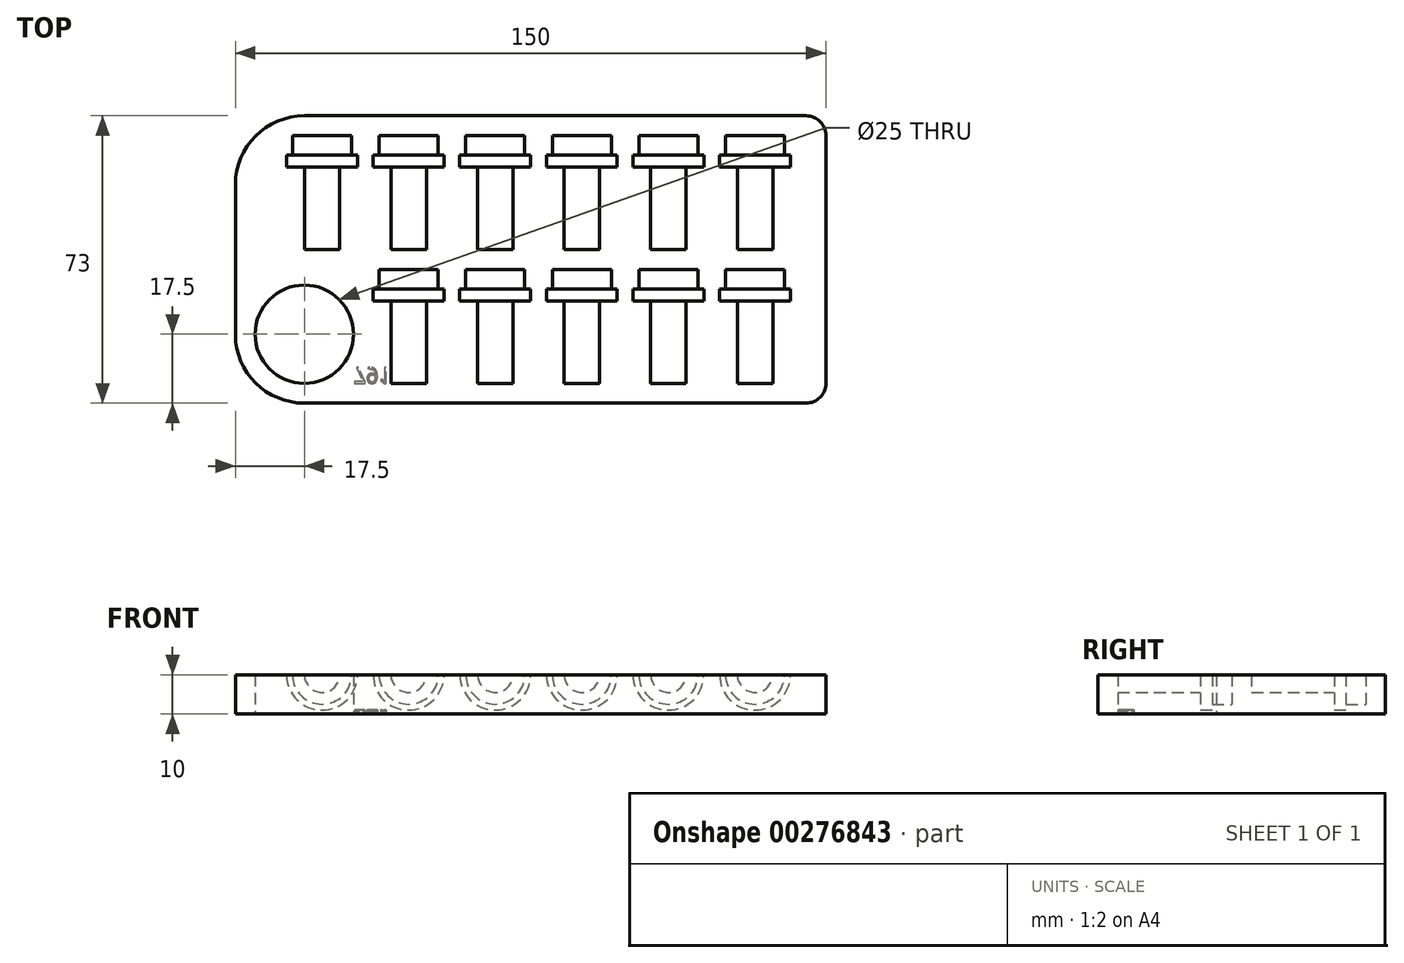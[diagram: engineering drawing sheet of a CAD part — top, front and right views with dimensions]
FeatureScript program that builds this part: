
annotation { "Feature Type Name" : "Feature", "Feature Type Description" : "" }
export const myFeature = defineFeature(function(context is Context, id is Id, definition is map)
    precondition{}
    {
        {
            var Q0;
            Q0=qCreatedBy(makeId("Top.planeOp"),FACE);
            var sketch = newSketch(context, id + "F0", { "sketchPlane" : qUnion([Q0])});
            skLineSegment(sketch, "E0.bottom", {"start": v(17.5, 0) * mm, "end": v(145, 0) * mm});
            skLineSegment(sketch, "E0.top", {"start": v(17.5, 73) * mm, "end": v(145, 73) * mm});
            skLineSegment(sketch, "E0.left", {"start": v(0, 17.5) * mm, "end": v(0, 55.5) * mm});
            skLineSegment(sketch, "E0.right", {"start": v(150, 5) * mm, "end": v(150, 68) * mm});
            skLineSegment(sketch, "E1.bottom", {"start": v(0, 0) * mm, "end": v(17.5, 0) * mm, "construction": true});
            skLineSegment(sketch, "E1.top", {"start": v(0, 17.5) * mm, "end": v(17.5, 17.5) * mm, "construction": true});
            skLineSegment(sketch, "E1.left", {"start": v(0, 0) * mm, "end": v(0, 17.5) * mm, "construction": true});
            skLineSegment(sketch, "E1.right", {"start": v(17.5, 0) * mm, "end": v(17.5, 17.5) * mm, "construction": true});
            skCircle(sketch, "E2", {"center": v(17.5, 17.5) * mm, "radius": 12.5 * mm});
            skPoint(sketch, "E3.visualSharp", {"position": v(0, 0) * mm});
            skArc(sketch, "E3.filletArc", {"start": v(0, 17.5) * mm, "mid": v(5.13, 5.13) * mm, "end": v(17.5, 0) * mm});
            skPoint(sketch, "E4.visualSharp", {"position": v(0, 73) * mm});
            skArc(sketch, "E4.filletArc", {"start": v(17.5, 73) * mm, "mid": v(5.13, 67.87) * mm, "end": v(0, 55.5) * mm});
            skPoint(sketch, "E5.visualSharp", {"position": v(150, 73) * mm});
            skArc(sketch, "E5.filletArc", {"start": v(150, 68) * mm, "mid": v(148.54, 71.54) * mm, "end": v(145, 73) * mm});
            skPoint(sketch, "E6.visualSharp", {"position": v(150, 0) * mm});
            skArc(sketch, "E6.filletArc", {"start": v(145, 0) * mm, "mid": v(148.54, 1.46) * mm, "end": v(150, 5) * mm});
            skSolve(sketch);
        }
        {
            var Q0;
            Q0=makeQuery(id+"F0.imprint","IMPRINT",FACE,{"disambiguationData":[TD([[makeQuery(id+"F0.imprint","IMPRINT",EDGE,{"derivedFrom":sQuery(id+"F0.wireOp",EDGE,"E0.bottom")}),1.0]])]});
            extrude(context, id + "F1", {"entities" : qUnion([Q0]), "depth" : 10 * mm});
        }
        {
            var Q0;
            Q0=makeQuery(id+"F1.opExtrude","CAP_FACE",FACE,{"disambiguationData":[OSD([sQuery(id+"F0.wireOp",EDGE,"E0.bottom"),sQuery(id+"F0.wireOp",EDGE,"E0.top"),sQuery(id+"F0.wireOp",EDGE,"E0.left"),sQuery(id+"F0.wireOp",EDGE,"E0.right"),sQuery(id+"F0.wireOp",EDGE,"E2"),sQuery(id+"F0.wireOp",EDGE,"E3.filletArc"),sQuery(id+"F0.wireOp",EDGE,"E4.filletArc"),sQuery(id+"F0.wireOp",EDGE,"E5.filletArc"),sQuery(id+"F0.wireOp",EDGE,"E6.filletArc")])],"isStart":false});
            var sketch = newSketch(context, id + "F2", { "sketchPlane" : qUnion([Q0])});
            skLineSegment(sketch, "E7.bottom", {"start": v(0, 0) * mm, "end": v(44, 0) * mm, "construction": true});
            skLineSegment(sketch, "E7.top", {"start": v(0, 5) * mm, "end": v(44, 5) * mm, "construction": true});
            skLineSegment(sketch, "E7.left", {"start": v(0, 0) * mm, "end": v(0, 5) * mm, "construction": true});
            skLineSegment(sketch, "E7.right", {"start": v(44, 0) * mm, "end": v(44, 5) * mm, "construction": true});
            skLineSegment(sketch, "E8", {"start": v(44, 5) * mm, "end": v(44, 39) * mm, "construction": true});
            skLineSegment(sketch, "E9", {"start": v(44, 39) * mm, "end": v(66, 39) * mm, "construction": true});
            skLineSegment(sketch, "E10", {"start": v(66, 39) * mm, "end": v(88, 39) * mm, "construction": true});
            skLineSegment(sketch, "E11", {"start": v(44, 39) * mm, "end": v(22, 39) * mm, "construction": true});
            skLineSegment(sketch, "E12", {"start": v(88, 39) * mm, "end": v(110, 39) * mm, "construction": true});
            skLineSegment(sketch, "E13", {"start": v(110, 39) * mm, "end": v(132, 39) * mm, "construction": true});
            skLineSegment(sketch, "E14", {"start": v(44, 5) * mm, "end": v(66, 5) * mm, "construction": true});
            skLineSegment(sketch, "E15", {"start": v(66, 5) * mm, "end": v(88, 5) * mm, "construction": true});
            skLineSegment(sketch, "E16", {"start": v(88, 5) * mm, "end": v(110, 5) * mm, "construction": true});
            skLineSegment(sketch, "E17", {"start": v(110, 5) * mm, "end": v(132, 5) * mm, "construction": true});
            skLineSegment(sketch, "E18.bottom", {"start": v(22, 39) * mm, "end": v(26.5, 39) * mm});
            skLineSegment(sketch, "E18.left", {"start": v(22, 39) * mm, "end": v(22, 60) * mm});
            skLineSegment(sketch, "E18.right", {"start": v(26.5, 39) * mm, "end": v(26.5, 60) * mm});
            skLineSegment(sketch, "E19.bottom", {"start": v(44, 39) * mm, "end": v(48.5, 39) * mm});
            skLineSegment(sketch, "E19.left", {"start": v(44, 39) * mm, "end": v(44, 60) * mm});
            skLineSegment(sketch, "E19.right", {"start": v(48.5, 39) * mm, "end": v(48.5, 60) * mm});
            skLineSegment(sketch, "E20.bottom", {"start": v(66, 39) * mm, "end": v(70.5, 39) * mm});
            skLineSegment(sketch, "E20.left", {"start": v(66, 39) * mm, "end": v(66, 60) * mm});
            skLineSegment(sketch, "E20.right", {"start": v(70.5, 39) * mm, "end": v(70.5, 60) * mm});
            skLineSegment(sketch, "E21.bottom", {"start": v(88, 39) * mm, "end": v(92.5, 39) * mm});
            skLineSegment(sketch, "E21.left", {"start": v(88, 39) * mm, "end": v(88, 60) * mm});
            skLineSegment(sketch, "E21.right", {"start": v(92.5, 39) * mm, "end": v(92.5, 60) * mm});
            skLineSegment(sketch, "E22.bottom", {"start": v(110, 39) * mm, "end": v(114.5, 39) * mm});
            skLineSegment(sketch, "E22.left", {"start": v(110, 39) * mm, "end": v(110, 60) * mm});
            skLineSegment(sketch, "E22.right", {"start": v(114.5, 39) * mm, "end": v(114.5, 60) * mm});
            skLineSegment(sketch, "E23.bottom", {"start": v(132, 39) * mm, "end": v(136.5, 39) * mm});
            skLineSegment(sketch, "E23.left", {"start": v(132, 39) * mm, "end": v(132, 60) * mm});
            skLineSegment(sketch, "E23.right", {"start": v(136.5, 39) * mm, "end": v(136.5, 60) * mm});
            skLineSegment(sketch, "E24.bottom", {"start": v(44, 5) * mm, "end": v(48.5, 5) * mm});
            skLineSegment(sketch, "E24.left", {"start": v(44, 5) * mm, "end": v(44, 26) * mm});
            skLineSegment(sketch, "E24.right", {"start": v(48.5, 5) * mm, "end": v(48.5, 26) * mm});
            skLineSegment(sketch, "E25.bottom", {"start": v(66, 5) * mm, "end": v(70.5, 5) * mm});
            skLineSegment(sketch, "E25.left", {"start": v(66, 5) * mm, "end": v(66, 26) * mm});
            skLineSegment(sketch, "E25.right", {"start": v(70.5, 5) * mm, "end": v(70.5, 26) * mm});
            skLineSegment(sketch, "E26.bottom", {"start": v(88, 5) * mm, "end": v(92.5, 5) * mm});
            skLineSegment(sketch, "E26.left", {"start": v(88, 5) * mm, "end": v(88, 26) * mm});
            skLineSegment(sketch, "E26.right", {"start": v(92.5, 5) * mm, "end": v(92.5, 26) * mm});
            skLineSegment(sketch, "E27.bottom", {"start": v(110, 5) * mm, "end": v(114.5, 5) * mm});
            skLineSegment(sketch, "E27.left", {"start": v(110, 5) * mm, "end": v(110, 26) * mm});
            skLineSegment(sketch, "E27.right", {"start": v(114.5, 5) * mm, "end": v(114.5, 26) * mm});
            skLineSegment(sketch, "E28.bottom", {"start": v(132, 5) * mm, "end": v(136.5, 5) * mm});
            skLineSegment(sketch, "E28.left", {"start": v(132, 5) * mm, "end": v(132, 26) * mm});
            skLineSegment(sketch, "E28.right", {"start": v(136.5, 5) * mm, "end": v(136.5, 26) * mm});
            skLineSegment(sketch, "E29.bottom", {"start": v(26.5, 60) * mm, "end": v(31, 60) * mm});
            skLineSegment(sketch, "E29.top", {"start": v(29.5, 63) * mm, "end": v(31, 63) * mm});
            skLineSegment(sketch, "E29.left", {"start": v(22, 60) * mm, "end": v(22, 63) * mm});
            skLineSegment(sketch, "E29.right", {"start": v(31, 60) * mm, "end": v(31, 63) * mm});
            skLineSegment(sketch, "E30.bottom", {"start": v(48.5, 60) * mm, "end": v(53, 60) * mm});
            skLineSegment(sketch, "E30.top", {"start": v(51.5, 63) * mm, "end": v(53, 63) * mm});
            skLineSegment(sketch, "E30.left", {"start": v(44, 60) * mm, "end": v(44, 63) * mm});
            skLineSegment(sketch, "E30.right", {"start": v(53, 60) * mm, "end": v(53, 63) * mm});
            skLineSegment(sketch, "E31.bottom", {"start": v(70.5, 60) * mm, "end": v(75, 60) * mm});
            skLineSegment(sketch, "E31.top", {"start": v(73.5, 63) * mm, "end": v(75, 63) * mm});
            skLineSegment(sketch, "E31.left", {"start": v(66, 60) * mm, "end": v(66, 63) * mm});
            skLineSegment(sketch, "E31.right", {"start": v(75, 60) * mm, "end": v(75, 63) * mm});
            skLineSegment(sketch, "E32.bottom", {"start": v(92.5, 60) * mm, "end": v(97, 60) * mm});
            skLineSegment(sketch, "E32.top", {"start": v(95.5, 63) * mm, "end": v(97, 63) * mm});
            skLineSegment(sketch, "E32.left", {"start": v(88, 60) * mm, "end": v(88, 63) * mm});
            skLineSegment(sketch, "E32.right", {"start": v(97, 60) * mm, "end": v(97, 63) * mm});
            skLineSegment(sketch, "E33.bottom", {"start": v(114.5, 60) * mm, "end": v(119, 60) * mm});
            skLineSegment(sketch, "E33.top", {"start": v(117.5, 63) * mm, "end": v(119, 63) * mm});
            skLineSegment(sketch, "E33.left", {"start": v(110, 60) * mm, "end": v(110, 63) * mm});
            skLineSegment(sketch, "E33.right", {"start": v(119, 60) * mm, "end": v(119, 63) * mm});
            skLineSegment(sketch, "E34.bottom", {"start": v(136.5, 60) * mm, "end": v(141, 60) * mm});
            skLineSegment(sketch, "E34.top", {"start": v(139.5, 63) * mm, "end": v(141, 63) * mm});
            skLineSegment(sketch, "E34.left", {"start": v(132, 60) * mm, "end": v(132, 63) * mm});
            skLineSegment(sketch, "E34.right", {"start": v(141, 60) * mm, "end": v(141, 63) * mm});
            skLineSegment(sketch, "E35.bottom", {"start": v(48.5, 26) * mm, "end": v(53, 26) * mm});
            skLineSegment(sketch, "E35.top", {"start": v(51.5, 29) * mm, "end": v(53, 29) * mm});
            skLineSegment(sketch, "E35.left", {"start": v(44, 26) * mm, "end": v(44, 29) * mm});
            skLineSegment(sketch, "E35.right", {"start": v(53, 26) * mm, "end": v(53, 29) * mm});
            skLineSegment(sketch, "E36.bottom", {"start": v(70.5, 26) * mm, "end": v(75, 26) * mm});
            skLineSegment(sketch, "E36.top", {"start": v(73.5, 29) * mm, "end": v(75, 29) * mm});
            skLineSegment(sketch, "E36.left", {"start": v(66, 26) * mm, "end": v(66, 29) * mm});
            skLineSegment(sketch, "E36.right", {"start": v(75, 26) * mm, "end": v(75, 29) * mm});
            skLineSegment(sketch, "E37.bottom", {"start": v(92.5, 26) * mm, "end": v(97, 26) * mm});
            skLineSegment(sketch, "E37.top", {"start": v(95.5, 29) * mm, "end": v(97, 29) * mm});
            skLineSegment(sketch, "E37.left", {"start": v(88, 26) * mm, "end": v(88, 29) * mm});
            skLineSegment(sketch, "E37.right", {"start": v(97, 26) * mm, "end": v(97, 29) * mm});
            skLineSegment(sketch, "E38.bottom", {"start": v(114.5, 26) * mm, "end": v(119, 26) * mm});
            skLineSegment(sketch, "E38.top", {"start": v(117.5, 29) * mm, "end": v(119, 29) * mm});
            skLineSegment(sketch, "E38.left", {"start": v(110, 26) * mm, "end": v(110, 29) * mm});
            skLineSegment(sketch, "E38.right", {"start": v(119, 26) * mm, "end": v(119, 29) * mm});
            skLineSegment(sketch, "E39.bottom", {"start": v(136.5, 26) * mm, "end": v(141, 26) * mm});
            skLineSegment(sketch, "E39.top", {"start": v(139.5, 29) * mm, "end": v(141, 29) * mm});
            skLineSegment(sketch, "E39.left", {"start": v(132, 26) * mm, "end": v(132, 29) * mm});
            skLineSegment(sketch, "E39.right", {"start": v(141, 26) * mm, "end": v(141, 29) * mm});
            skLineSegment(sketch, "E40.top", {"start": v(22, 68) * mm, "end": v(29.5, 68) * mm});
            skLineSegment(sketch, "E40.left", {"start": v(22, 63) * mm, "end": v(22, 68) * mm});
            skLineSegment(sketch, "E40.right", {"start": v(29.5, 63) * mm, "end": v(29.5, 68) * mm});
            skLineSegment(sketch, "E41.top", {"start": v(44, 68) * mm, "end": v(51.5, 68) * mm});
            skLineSegment(sketch, "E41.left", {"start": v(44, 63) * mm, "end": v(44, 68) * mm});
            skLineSegment(sketch, "E41.right", {"start": v(51.5, 63) * mm, "end": v(51.5, 68) * mm});
            skLineSegment(sketch, "E42.top", {"start": v(66, 68) * mm, "end": v(73.5, 68) * mm});
            skLineSegment(sketch, "E42.left", {"start": v(66, 63) * mm, "end": v(66, 68) * mm});
            skLineSegment(sketch, "E42.right", {"start": v(73.5, 63) * mm, "end": v(73.5, 68) * mm});
            skLineSegment(sketch, "E43.top", {"start": v(88, 68) * mm, "end": v(95.5, 68) * mm});
            skLineSegment(sketch, "E43.left", {"start": v(88, 63) * mm, "end": v(88, 68) * mm});
            skLineSegment(sketch, "E43.right", {"start": v(95.5, 63) * mm, "end": v(95.5, 68) * mm});
            skLineSegment(sketch, "E44.top", {"start": v(110, 68) * mm, "end": v(117.5, 68) * mm});
            skLineSegment(sketch, "E44.left", {"start": v(110, 63) * mm, "end": v(110, 68) * mm});
            skLineSegment(sketch, "E44.right", {"start": v(117.5, 63) * mm, "end": v(117.5, 68) * mm});
            skLineSegment(sketch, "E45.top", {"start": v(132, 68) * mm, "end": v(139.5, 68) * mm});
            skLineSegment(sketch, "E45.left", {"start": v(132, 63) * mm, "end": v(132, 68) * mm});
            skLineSegment(sketch, "E45.right", {"start": v(139.5, 63) * mm, "end": v(139.5, 68) * mm});
            skLineSegment(sketch, "E46.top", {"start": v(132, 34) * mm, "end": v(139.5, 34) * mm});
            skLineSegment(sketch, "E46.left", {"start": v(132, 29) * mm, "end": v(132, 34) * mm});
            skLineSegment(sketch, "E46.right", {"start": v(139.5, 29) * mm, "end": v(139.5, 34) * mm});
            skLineSegment(sketch, "E47.top", {"start": v(110, 34) * mm, "end": v(117.5, 34) * mm});
            skLineSegment(sketch, "E47.left", {"start": v(110, 29) * mm, "end": v(110, 34) * mm});
            skLineSegment(sketch, "E47.right", {"start": v(117.5, 29) * mm, "end": v(117.5, 34) * mm});
            skLineSegment(sketch, "E48.top", {"start": v(88, 34) * mm, "end": v(95.5, 34) * mm});
            skLineSegment(sketch, "E48.left", {"start": v(88, 29) * mm, "end": v(88, 34) * mm});
            skLineSegment(sketch, "E48.right", {"start": v(95.5, 29) * mm, "end": v(95.5, 34) * mm});
            skLineSegment(sketch, "E49.top", {"start": v(66, 34) * mm, "end": v(73.5, 34) * mm});
            skLineSegment(sketch, "E49.left", {"start": v(66, 29) * mm, "end": v(66, 34) * mm});
            skLineSegment(sketch, "E49.right", {"start": v(73.5, 29) * mm, "end": v(73.5, 34) * mm});
            skLineSegment(sketch, "E50.top", {"start": v(44, 34) * mm, "end": v(51.5, 34) * mm});
            skLineSegment(sketch, "E50.left", {"start": v(44, 29) * mm, "end": v(44, 34) * mm});
            skLineSegment(sketch, "E50.right", {"start": v(51.5, 29) * mm, "end": v(51.5, 34) * mm});
            skSolve(sketch);
        }
        {
            var Q0;
            Q0=makeQuery(id+"F2.imprint","IMPRINT",FACE,{"disambiguationData":[TD([[makeQuery(id+"F2.imprint","IMPRINT",EDGE,{"derivedFrom":sQuery(id+"F2.wireOp",EDGE,"E18.bottom")}),1.0]])]});
            var Q1;
            Q1=sQuery(id+"F2.wireOp",EDGE,"E18.left");
            revolve(context, id + "F3", {"operationType" : NewBodyOperationType.REMOVE, "entities" : qUnion([Q0]), "axis" : qUnion([Q1]), "revolveType" : RevolveType.FULL, "oppositeDirection" : true});
        }
        {
            var Q0;
            Q0=makeQuery(id+"F2.imprint","IMPRINT",FACE,{"disambiguationData":[TD([[makeQuery(id+"F2.imprint","IMPRINT",EDGE,{"derivedFrom":sQuery(id+"F2.wireOp",EDGE,"E24.bottom")}),1.0]])]});
            var Q1;
            Q1=makeQuery(id+"F2.imprint","IMPRINT",FACE,{"disambiguationData":[TD([[makeQuery(id+"F2.imprint","IMPRINT",EDGE,{"derivedFrom":sQuery(id+"F2.wireOp",EDGE,"E19.bottom")}),1.0]])]});
            var Q2;
            Q2=sQuery(id+"F2.wireOp",EDGE,"E19.left");
            revolve(context, id + "F4", {"operationType" : NewBodyOperationType.REMOVE, "entities" : qUnion([Q0, Q1]), "axis" : qUnion([Q2]), "revolveType" : RevolveType.FULL, "oppositeDirection" : true});
        }
        {
            var Q0;
            Q0=makeQuery(id+"F2.imprint","IMPRINT",FACE,{"disambiguationData":[TD([[makeQuery(id+"F2.imprint","IMPRINT",EDGE,{"derivedFrom":sQuery(id+"F2.wireOp",EDGE,"E25.bottom")}),1.0]])]});
            var Q1;
            Q1=makeQuery(id+"F2.imprint","IMPRINT",FACE,{"disambiguationData":[TD([[makeQuery(id+"F2.imprint","IMPRINT",EDGE,{"derivedFrom":sQuery(id+"F2.wireOp",EDGE,"E20.bottom")}),1.0]])]});
            var Q2;
            Q2=sQuery(id+"F2.wireOp",EDGE,"E20.left");
            revolve(context, id + "F5", {"operationType" : NewBodyOperationType.REMOVE, "entities" : qUnion([Q0, Q1]), "axis" : qUnion([Q2]), "revolveType" : RevolveType.FULL, "oppositeDirection" : true});
        }
        {
            var Q0;
            Q0=makeQuery(id+"F2.imprint","IMPRINT",FACE,{"disambiguationData":[TD([[makeQuery(id+"F2.imprint","IMPRINT",EDGE,{"derivedFrom":sQuery(id+"F2.wireOp",EDGE,"E26.bottom")}),1.0]])]});
            var Q1;
            Q1=makeQuery(id+"F2.imprint","IMPRINT",FACE,{"disambiguationData":[TD([[makeQuery(id+"F2.imprint","IMPRINT",EDGE,{"derivedFrom":sQuery(id+"F2.wireOp",EDGE,"E21.bottom")}),1.0]])]});
            var Q2;
            Q2=sQuery(id+"F2.wireOp",EDGE,"E21.left");
            revolve(context, id + "F6", {"operationType" : NewBodyOperationType.REMOVE, "entities" : qUnion([Q0, Q1]), "axis" : qUnion([Q2]), "revolveType" : RevolveType.FULL, "oppositeDirection" : true});
        }
        {
            var Q0;
            Q0=makeQuery(id+"F2.imprint","IMPRINT",FACE,{"disambiguationData":[TD([[makeQuery(id+"F2.imprint","IMPRINT",EDGE,{"derivedFrom":sQuery(id+"F2.wireOp",EDGE,"E27.bottom")}),1.0]])]});
            var Q1;
            Q1=makeQuery(id+"F2.imprint","IMPRINT",FACE,{"disambiguationData":[TD([[makeQuery(id+"F2.imprint","IMPRINT",EDGE,{"derivedFrom":sQuery(id+"F2.wireOp",EDGE,"E22.bottom")}),1.0]])]});
            var Q2;
            Q2=sQuery(id+"F2.wireOp",EDGE,"E22.left");
            revolve(context, id + "F7", {"operationType" : NewBodyOperationType.REMOVE, "entities" : qUnion([Q0, Q1]), "axis" : qUnion([Q2]), "revolveType" : RevolveType.FULL, "oppositeDirection" : true});
        }
        {
            var Q0;
            Q0=makeQuery(id+"F2.imprint","IMPRINT",FACE,{"disambiguationData":[TD([[makeQuery(id+"F2.imprint","IMPRINT",EDGE,{"derivedFrom":sQuery(id+"F2.wireOp",EDGE,"E28.bottom")}),1.0]])]});
            var Q1;
            Q1=makeQuery(id+"F2.imprint","IMPRINT",FACE,{"disambiguationData":[TD([[makeQuery(id+"F2.imprint","IMPRINT",EDGE,{"derivedFrom":sQuery(id+"F2.wireOp",EDGE,"E23.bottom")}),1.0]])]});
            var Q2;
            Q2=sQuery(id+"F2.wireOp",EDGE,"E23.left");
            revolve(context, id + "F8", {"operationType" : NewBodyOperationType.REMOVE, "entities" : qUnion([Q0, Q1]), "axis" : qUnion([Q2]), "revolveType" : RevolveType.FULL, "oppositeDirection" : true});
        }
        {
            var Q0;
            Q0=makeQuery(id+"F1.opExtrude","CAP_FACE",FACE,{"disambiguationData":[OSD([sQuery(id+"F0.wireOp",EDGE,"E0.bottom"),sQuery(id+"F0.wireOp",EDGE,"E0.top"),sQuery(id+"F0.wireOp",EDGE,"E0.left"),sQuery(id+"F0.wireOp",EDGE,"E0.right"),sQuery(id+"F0.wireOp",EDGE,"E2"),sQuery(id+"F0.wireOp",EDGE,"E3.filletArc"),sQuery(id+"F0.wireOp",EDGE,"E4.filletArc"),sQuery(id+"F0.wireOp",EDGE,"E5.filletArc"),sQuery(id+"F0.wireOp",EDGE,"E6.filletArc")])],"isStart":true});
            var sketch = newSketch(context, id + "F9", { "sketchPlane" : qUnion([Q0])});
            skLineSegment(sketch, "E51.bottom", {"start": v(0, 0) * mm, "end": v(30, 0) * mm, "construction": true});
            skLineSegment(sketch, "E51.top", {"start": v(0, -5) * mm, "end": v(30, -5) * mm, "construction": true});
            skLineSegment(sketch, "E51.left", {"start": v(0, 0) * mm, "end": v(0, -5) * mm, "construction": true});
            skLineSegment(sketch, "E51.right", {"start": v(30, 0) * mm, "end": v(30, -5) * mm, "construction": true});
            skText(sketch, "E52", { "text": "791", "fontName": "OpenSans-Regular.ttf"});
            const initialGuessF9  = {"E52": [0.03, -0.009, 1, 0, 0.004]};
            skSetInitialGuess(sketch, initialGuessF9);
            skSolve(sketch);
        }
        {
            var Q0;
            Q0 = qSketchRegion(id + "F9", true);
            extrude(context, id + "F10", {"entities" : qUnion([Q0]), "operationType" : NewBodyOperationType.REMOVE, "oppositeDirection" : true, "depth" : 1 * mm});
        }
    });
